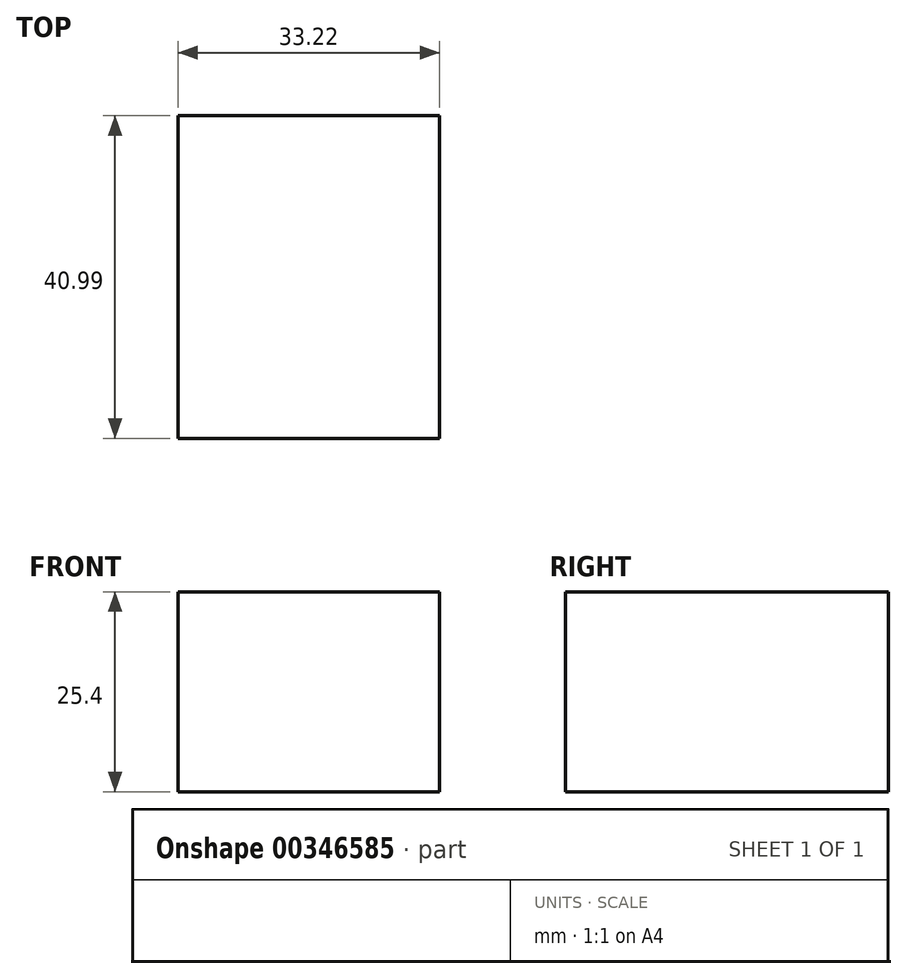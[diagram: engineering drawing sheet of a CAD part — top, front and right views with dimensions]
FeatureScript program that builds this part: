
annotation { "Feature Type Name" : "Feature", "Feature Type Description" : "" }
export const myFeature = defineFeature(function(context is Context, id is Id, definition is map)
    precondition{}
    {
        {
            var Q0;
            Q0=qCreatedBy(makeId("Top.planeOp"),FACE);
            var sketch = newSketch(context, id + "F0", { "sketchPlane" : qUnion([Q0])});
            skLineSegment(sketch, "E0.bottom", {"start": v(-37.4, 0) * mm, "end": v(-70.62, 0) * mm});
            skLineSegment(sketch, "E0.top", {"start": v(-37.4, -41) * mm, "end": v(-70.62, -41) * mm});
            skLineSegment(sketch, "E0.left", {"start": v(-37.4, 0) * mm, "end": v(-37.4, -41) * mm});
            skLineSegment(sketch, "E0.right", {"start": v(-70.62, 0) * mm, "end": v(-70.62, -41) * mm});
            skPoint(sketch, "E0.middle", {"position": v(-54, -20.5) * mm});
            skSolve(sketch);
        }
        {
            var Q0;
            Q0 = qSketchRegion(id + "F0", true);
            var Q1;
            Q1=makeQuery(id+"F0.imprint","IMPRINT",FACE,{"disambiguationData":[TD([[makeQuery(id+"F0.imprint","IMPRINT",EDGE,{"derivedFrom":sQuery(id+"F0.wireOp",EDGE,"E0.bottom")}),1.0]])]});
            extrude(context, id + "F1", {"entities" : qUnion([Q0, Q1]), "depth" : 25.4 * mm});
        }
    });
